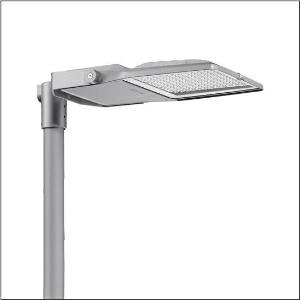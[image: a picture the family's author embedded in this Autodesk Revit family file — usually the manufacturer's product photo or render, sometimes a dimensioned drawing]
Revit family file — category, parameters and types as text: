
# Revit family: floodlight_fl_21_iq_midi___pl43_5xa7781f2a3a_7a49
name_source: partatom
category: Lighting Fixtures
units: mm (PartAtom-declared; Revit-internal decimal feet)

## family parameters
Cut with Voids When Loaded = No
Host = Face
Light Source = No
Part Type = Normal
Room Calculation Point = No
Round Connector Dimension = Use Diameter
Shared = No

## types (1)
- --- (1 x LED, 36680 lm, 270.2 W, 3000K)
    Apparent Load = 270 VA
    CIE Flux Codes = 27 78 99 100 100
    Color Rendering = 70
    Color Temperature = 3000K
    Default Elevation = 1800 mm
    Description = Floodlight FL 21 iQ midi, floodlight, primary light control with lens, of PMMA, primary optical cover: protective disc, of toughened safety glass, transparent, light distribution: PL43, light emission: direct distribution, installation type: surface-mounted, LED, High Power LED, rated luminous flux: 36.680lm, luminous efficacy: 136lm/W, light colour: 730, colour temperature: 3000K, control gear: ECG iQ, control: optimised constant luminous flux control (CLO 2.0), Desk-Remote (wireless, voltage-free reading and setting of iQ features in the workshop via application-optimized NFC function/RFID function), Light-Fading, Smart-Wire, Night-Set, Lumen-Switch, Temp-Guard, Auto-Match, with terminal, 6-pole, mains connection: 220..240V, AC, 50/60Hz, start of lifetime: 270W, end of service life: 287W, reduction: 117W, luminaire housing, of diecast aluminium, powder-coated, Siteco® metallic grey (DB 702S), corrosivity category C5 mid according to DIN EN ISO 12944, sealing non-destructively replaceable, please order mast flange separately, mast bracket, of steel, galvanised, powder-coated, Siteco® metallic grey (DB 702S), protection rating (complete): IP66, insulation class (complete): insulation class II (safety insulation), certification: CE, protection symbol: D, impact resistance: IK08, permissible operating ambient temperature: -40..+40°C, permissible operating ambient temperature for outdoor applications: -40..+50°C, standard: DIN EN 12944, LABS conformity tested according to VDMA 24364:2018-05, packaging unit: 1 piece

Light Distribution: PL43
    Height = 76 mm
    Lamp = 1 x LED
    Lamp Light Flux = 36680 lm
    Lamp Power = 270.2 W
    Lamp count = 1
    Length = 657 mm
    Luminous efficacy = 136 lm/W
    Manufacturer = Siteco
    ModVariant = No
    Model = 5XA7781F2A3A
    Number of Poles = 1
    OnlyDefault = Yes
    Power Factor = 1
    Product Name = Floodlight FL 21 iQ midi | PL43
    Product group = floodlight | pylon annexe
    ProductGroupID = 6200
    Protection Class = Protection class II
    Protection Degree = IP 66
    RLX_Detail_Level = 1
    RLX_Emergency_Light_Flux = 0 lm
    RLX_Emergency_Type = 0
    RLX_Emergency_Type_DB = No
    RlxData = <blob elided: 153681 chars, md5=c89fcb03>
    Socket = socket
    Standby Power = 0 W
    System Light Flux = 36680 lm
    System Power = 270 W
    Type Comments = factory setting: luminous flux: 100 % | dim-lin: 254 | 620 mA
    Type Image = l_1007123.jpg
    URL = http://relux.com
    VarID = @adj_053173
    Voltage = 0 V
    Weight = 0.00 kg
    Width = 442 mm

## geometry (parser evidence)
native form markers: Blend x4, Sweep x12
no freeform markers — native parametric forms only
